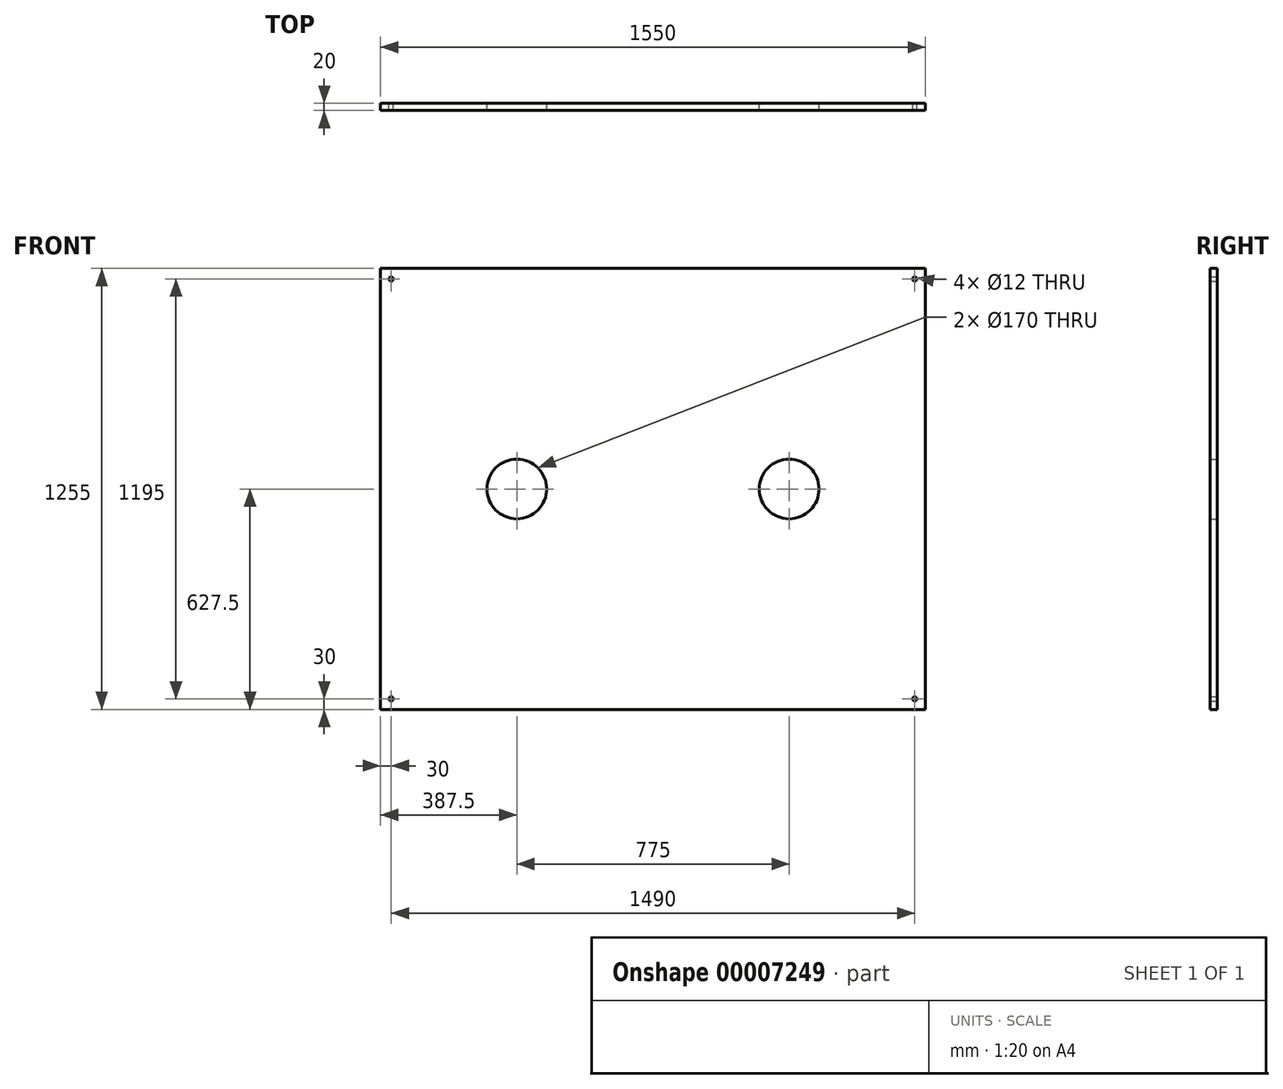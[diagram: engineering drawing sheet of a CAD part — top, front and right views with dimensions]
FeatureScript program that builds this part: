
annotation { "Feature Type Name" : "Feature", "Feature Type Description" : "" }
export const myFeature = defineFeature(function(context is Context, id is Id, definition is map)
    precondition{}
    {
        {
            var Q0;
            Q0=qCreatedBy(makeId("Front.planeOp"),FACE);
            var sketch = newSketch(context, id + "F0", { "sketchPlane" : qUnion([Q0])});
            skLineSegment(sketch, "E0.bottom", {"start": v(-775, 627.5) * mm, "end": v(775, 627.5) * mm});
            skLineSegment(sketch, "E0.top", {"start": v(-775, -627.5) * mm, "end": v(775, -627.5) * mm});
            skLineSegment(sketch, "E0.left", {"start": v(-775, 627.5) * mm, "end": v(-775, -627.5) * mm});
            skLineSegment(sketch, "E0.right", {"start": v(775, 627.5) * mm, "end": v(775, -627.5) * mm});
            skCircle(sketch, "E1", {"center": v(-745, 597.5) * mm, "radius": 6 * mm});
            skCircle(sketch, "E2", {"center": v(745, 597.5) * mm, "radius": 6 * mm});
            skCircle(sketch, "E3", {"center": v(-745, -597.5) * mm, "radius": 6 * mm});
            skCircle(sketch, "E4", {"center": v(745, -597.5) * mm, "radius": 6 * mm});
            skCircle(sketch, "E5", {"center": v(-387.5, 0) * mm, "radius": 85 * mm});
            skCircle(sketch, "E6", {"center": v(387.5, 0) * mm, "radius": 85 * mm});
            skSolve(sketch);
        }
        {
            var Q0;
            Q0=makeQuery(id+"F0.imprint","IMPRINT",FACE,{"disambiguationData":[TD([[makeQuery(id+"F0.imprint","IMPRINT",EDGE,{"derivedFrom":sQuery(id+"F0.wireOp",EDGE,"E0.bottom")}),-1.0]])]});
            extrude(context, id + "F1", {"entities" : qUnion([Q0]), "depth" : 20 * mm});
        }
    });
